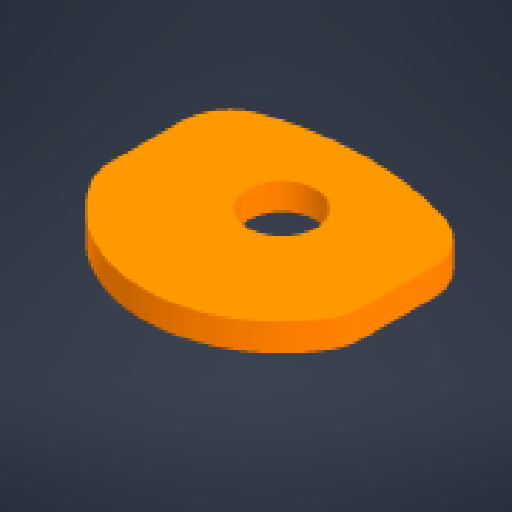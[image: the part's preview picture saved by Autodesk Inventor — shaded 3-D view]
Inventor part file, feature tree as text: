
AUTODESK INVENTOR PART (.ipt)
format: ipt  version: 2024 (Build 280153000, 153)  size: 162,304 bytes
history: native  units: mm
features: reference x10, other x4, extrude x2, sketch x2
ambient origin geometry x8: Origin, YZ Plane, XZ Plane, XY Plane, X Axis, Y Axis, Z Axis, Center Point
bodies: Body1 (feature_tree)
feature tree (18):
  other  "Твердое тело1"
  extrude  "Выдавливание1"  Depth=3.0mm TaperAngle=0.0deg
  extrude  "Выдавливание2"  Depth=7.0mm
  sketch  "Эскиз1"
  reference  "Ссылка1"
  sketch  "Эскиз2"
  reference  "Ссылка2"
  reference  "Ссылка3"
  reference  "Ссылка4"
  reference  "Ссылка5"
  reference  "Ссылка6"
  reference  "Ссылка7"
  reference  "Ссылка8"
  reference  "Ссылка9"
  reference  "Ссылка10"
  parser-record x1  (decoder bookkeeping rows leaked as tree rows — omitted from the tree; the rows remain in map.json)
  other  "arm_holder.iam"
  other  "arm_holder:1"
note: 1 file-system path scrubbed to <path> (originals preserved in map.json)
